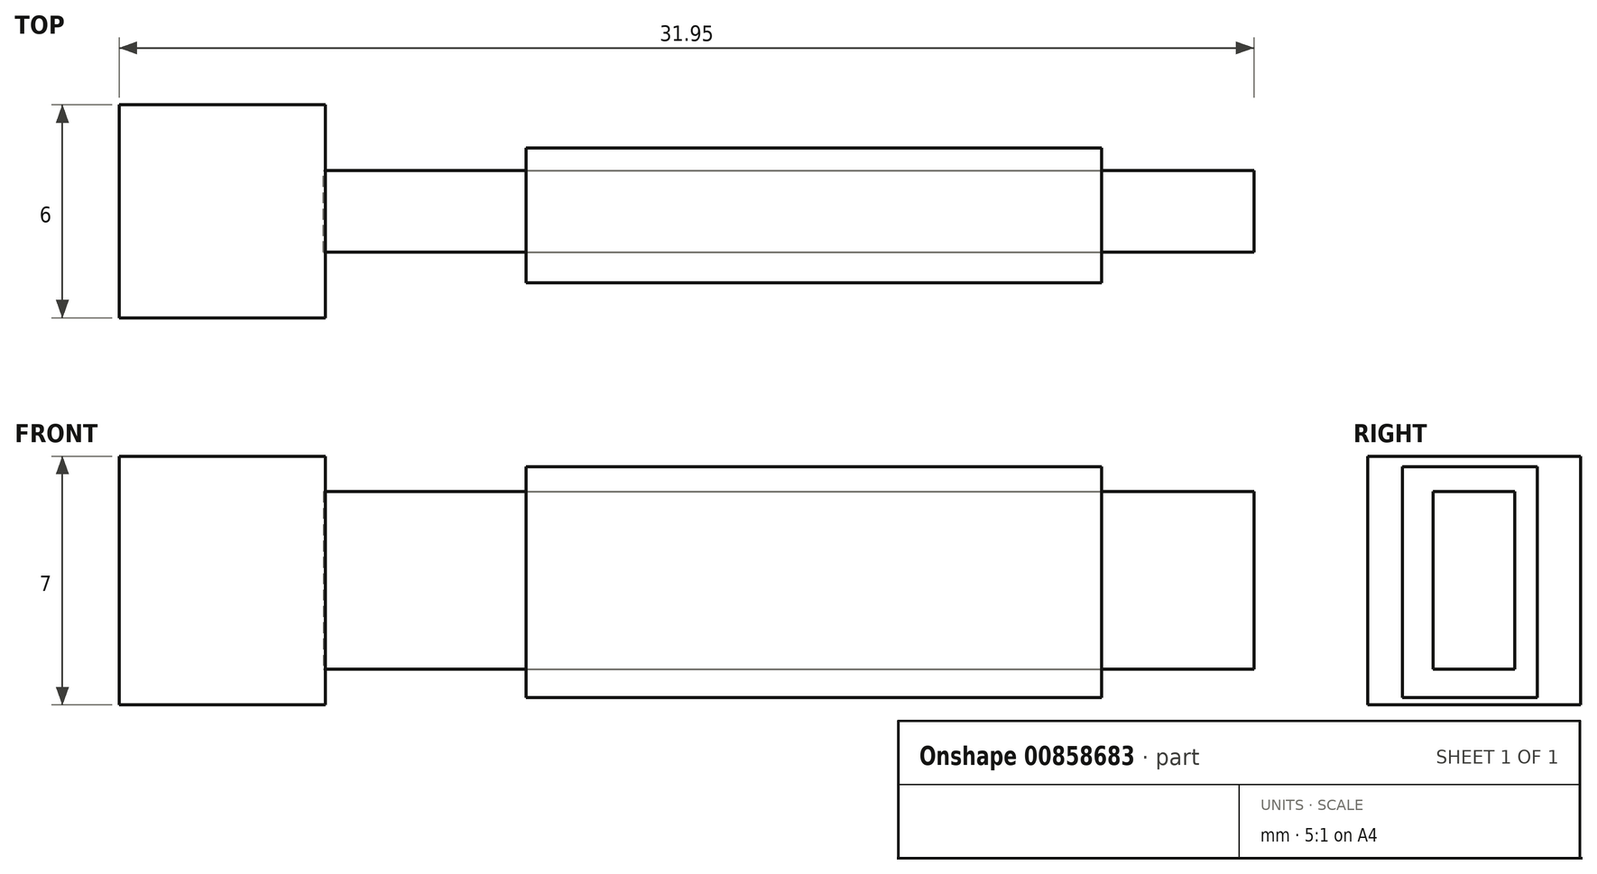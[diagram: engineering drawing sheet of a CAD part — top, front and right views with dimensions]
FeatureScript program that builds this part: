
annotation { "Feature Type Name" : "Feature", "Feature Type Description" : "" }
export const myFeature = defineFeature(function(context is Context, id is Id, definition is map)
    precondition{}
    {
        {
            var Q0;
            Q0=qCreatedBy(makeId("Top.planeOp"),FACE);
            var sketch = newSketch(context, id + "F0", { "sketchPlane" : qUnion([Q0])});
            skLineSegment(sketch, "E0.bottom", {"start": v(0, 0) * mm, "end": v(5.8, 0) * mm});
            skLineSegment(sketch, "E0.top", {"start": v(0, 6) * mm, "end": v(5.8, 6) * mm});
            skLineSegment(sketch, "E0.left", {"start": v(0, 0) * mm, "end": v(0, 6) * mm});
            skLineSegment(sketch, "E0.right", {"start": v(5.8, 0) * mm, "end": v(5.8, 6) * mm});
            skLineSegment(sketch, "E1.bottom", {"start": v(9.45, 1.85) * mm, "end": v(35.65, 1.85) * mm});
            skLineSegment(sketch, "E1.top", {"start": v(9.45, 4.15) * mm, "end": v(35.65, 4.15) * mm});
            skLineSegment(sketch, "E1.left", {"start": v(9.45, 1.85) * mm, "end": v(9.45, 4.15) * mm});
            skLineSegment(sketch, "E1.right", {"start": v(35.65, 1.85) * mm, "end": v(35.65, 4.15) * mm});
            skLineSegment(sketch, "E2.bottom", {"start": v(14.46, 8.99) * mm, "end": v(30.66, 8.99) * mm});
            skLineSegment(sketch, "E2.top", {"start": v(14.46, 5.19) * mm, "end": v(30.66, 5.19) * mm});
            skLineSegment(sketch, "E2.left", {"start": v(14.46, 8.99) * mm, "end": v(14.46, 5.19) * mm});
            skLineSegment(sketch, "E2.right", {"start": v(30.66, 8.99) * mm, "end": v(30.66, 5.19) * mm});
            skSolve(sketch);
        }
        {
            var Q0;
            Q0=makeQuery(id+"F0.imprint","IMPRINT",FACE,{"disambiguationData":[TD([[makeQuery(id+"F0.imprint","IMPRINT",EDGE,{"derivedFrom":sQuery(id+"F0.wireOp",EDGE,"E0.bottom")}),1.0]])]});
            extrude(context, id + "F1", {"entities" : qUnion([Q0]), "depth" : 7 * mm, "offsetDistance" : 25 * mm});
        }
        {
            var Q0;
            Q0=makeQuery(id+"F0.imprint","IMPRINT",FACE,{"disambiguationData":[TD([[makeQuery(id+"F0.imprint","IMPRINT",EDGE,{"derivedFrom":sQuery(id+"F0.wireOp",EDGE,"E1.bottom")}),1.0]])]});
            extrude(context, id + "F2", {"entities" : qUnion([Q0]), "depth" : 5 * mm, "offsetDistance" : 25 * mm});
        }
        {
            var Q0;
            Q0=makeQuery(id+"F0.imprint","IMPRINT",FACE,{"disambiguationData":[TD([[makeQuery(id+"F0.imprint","IMPRINT",EDGE,{"derivedFrom":sQuery(id+"F0.wireOp",EDGE,"E2.bottom")}),-1.0]])]});
            extrude(context, id + "F3", {"entities" : qUnion([Q0]), "depth" : 6.5 * mm, "offsetDistance" : 25 * mm});
        }
        {
            var Q0;
            Q0=makeQuery(id+"F2.opExtrude","SWEPT_BODY",BODY,{"disambiguationData":[OSD([sQuery(id+"F0.wireOp",EDGE,"E1.bottom"),sQuery(id+"F0.wireOp",EDGE,"E1.top"),sQuery(id+"F0.wireOp",EDGE,"E1.left"),sQuery(id+"F0.wireOp",EDGE,"E1.right")])]});
            transform(context, id + "F4", {"entities" : qUnion([Q0]), "transformType" : TransformType.TRANSLATION_3D, "dx" : -3.7 * mm, "dy" : 0 * mm, "dz" : 1 * mm, "makeCopy" : false});
        }
        {
            var Q0;
            Q0=makeQuery(id+"F3.opExtrude","SWEPT_BODY",BODY,{"disambiguationData":[OSD([sQuery(id+"F0.wireOp",EDGE,"E2.bottom"),sQuery(id+"F0.wireOp",EDGE,"E2.top"),sQuery(id+"F0.wireOp",EDGE,"E2.left"),sQuery(id+"F0.wireOp",EDGE,"E2.right")])]});
            transform(context, id + "F5", {"entities" : qUnion([Q0]), "transformType" : TransformType.TRANSLATION_3D, "dx" : -3 * mm, "dy" : -4.2 * mm, "dz" : 0.2 * mm, "makeCopy" : false});
        }
    });
